# Revit family: P710099-009
name_source: partatom
category: Lighting Fixtures
units: mm (PartAtom-declared; Revit-internal decimal feet)

## family parameters
Cut with Voids When Loaded = No
Host = Face
Light Source = Yes
OmniClass Number = 23.80.70.11.14.17
OmniClass Title = Direct/Indirect
Part Type = Normal
Room Calculation Point = No
Round Connector Dimension = Use Diameter
Shared = Yes

## types (1)
- P710099-009
    Apparent Load = 60 VA
    Assembly Code = D5020200
    Color Filter = 16777215
    Connector Description = Lighting Connector
    Default Elevation = 48 "
    Description = Mill Beam Collection One-Light Brushed Nickel/Faux Concrete Industrial Style Wall Light
    Dimming Lamp Color Temperature Shift = <None>
    Features = Give an unexpected artisanal edginess with the Mill Beam Collection 1-Light Brushed Nickel Industrial Wall Light. The slab silhouette is coated in a faux concrete finish accented by a brushed nickel backplate to create the perfect blend of organic and industrial character.
Application: Give an unexpected artisanal edginess with the Mill Beam Collection 1-Light Brushed Nickel Industrial Wall Light ideal for any entryway, hallway, foyer, bedroom, sitting room, living room, or bathroom.
Styles: Perfect for urban industrial and farmhouse style settings.
Finish: The slab silhouette is coated in a faux concrete finish accented by a brushed nickel backplate to create the perfect blend of organic and industrial character.
Materials: Constructed from steel to ensure a long product lifespan
mount the light fixture horizontally or vertically.
Glass/Shades: We recommend using vintage bulbs to enhance the light fixture's rustic aesthetic.
Bulbs: For ideal illumination, use 1 medium base bulb that is sold separately (60w max - LED/CFL/incandescent). Compatible with dimmable bulbs.
Dimensions: Measures 4-3/4-inch width by 7-1/8-inch height.
Certifications: cETLus Damp Location Listed.
Pairs With: Pairs with the Hemsworth, Bonn, and Foster collections by Progress Lighting.
Warranty: Our 1-Year Limited Warranty guarantees your complete satisfaction with your purchase and includes professional after-sales customer service support.
    Fixture distribution = Direct
    Glass = Paint - Hubbell - White Texture
    Gold = Hubbell - Gold
    Housing Material = Paint - Hubbell - Light Silver
    Lamp = LED/CFL/incandescent
    Load Classification = Lighting
    Manufacturer = Progress Lighting
    Model = P710099-009
    Photometric Web File = generic
    Power Factor = 1
    Product Documentation Link = https://hubbellcdn.com
    Product Link = https://www.hubbell.com
    Support = Paint - Hubbell - Dark Nickel
    Tilt Angle = 60.00°
    URL = https://www.hubbell.com
    Voltage = 120 V
    Warranty = 1 year Warranty
    Wattage Comments = 60W
    Watts = 60 W

## geometry (parser evidence)
native form markers: Sweep x4
no freeform markers — native parametric forms only
